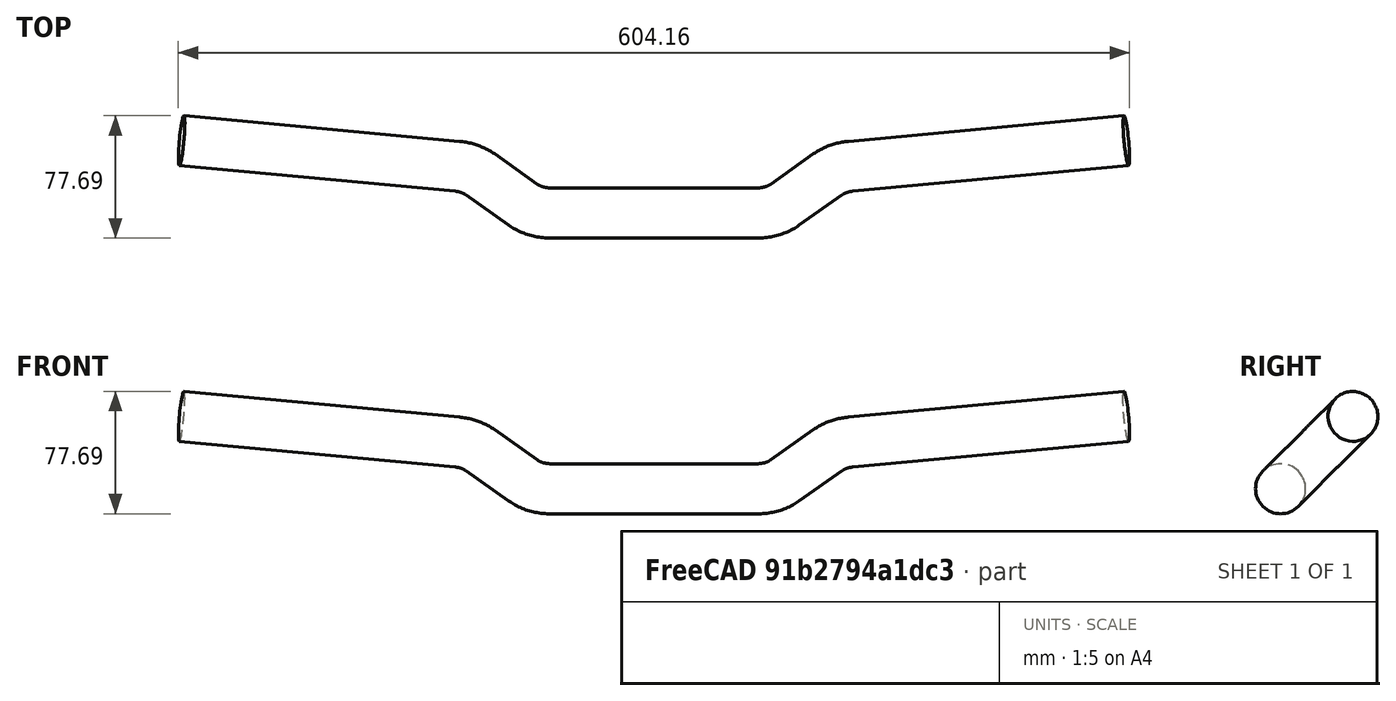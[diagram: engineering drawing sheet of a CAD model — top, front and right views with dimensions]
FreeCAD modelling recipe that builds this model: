
FCSTD DOCUMENT  (FreeCAD 0.20R27319 (Git))
Label: Riserbar_Single
License: All rights reserved
LicenseURL: http://en.wikipedia.org/wiki/All_rights_reserved
objects: Sketcher::SketchObject×2, PartDesign::AdditivePipe×1, PartDesign::Line×1, PartDesign::Plane×1, PartDesign::Body×1
note: 7 computed .brp shape members not serialized (recipe doc carries the construction recipe); baked Part::Feature solids carry a one-line shape summary decoded from their .brp

FEATURE [Sketcher::SketchObject] Sketch001  label="Profil"
  FullyConstrained = true
  MapMode = 5
  Placement = pos=(0,0,0) rot=(0.57735,0.57735,0.57735;2.0944rad)
  Support = -> [YZ_Plane]
  sketch-geometry (1):
    g0: Circle CenterX=0 CenterY=0 CenterZ=0 NormalX=0 NormalY=0 NormalZ=1 AngleXU=0 Radius=15.9
  constraints (2):
    c: Coincident(g0,g-1)
    c: Diameter(g0) = 31.8
FEATURE [Sketcher::SketchObject] Sketch  label="Lenker"
  FullyConstrained = true
  MapMode = 5
  Support = -> [XY_Plane]
  sketch-geometry (11):
    g0: LineSegment StartX=-300 StartY=65 StartZ=0 EndX=-125 EndY=41.9608 EndZ=0
    g1: LineSegment StartX=-110.585 StartY=34.8524 StartZ=0 EndX=-83.0555 EndY=7.32233 EndZ=0
    g2: LineSegment StartX=-65.3778 StartY=0 StartZ=0 EndX=65.3778 EndY=0 EndZ=0
    g3: LineSegment StartX=83.0555 StartY=7.32233 StartZ=0 EndX=110.585 EndY=34.8524 EndZ=0
    g4: LineSegment StartX=125 StartY=41.9608 StartZ=0 EndX=300 EndY=65 EndZ=0
    g5: ArcOfCircle CenterX=-128.263 CenterY=17.1747 CenterZ=0 NormalX=0 NormalY=0 NormalZ=1 AngleXU=0 Radius=25 StartAngle=0.785398 EndAngle=1.4399
    g6: ArcOfCircle CenterX=128.263 CenterY=17.1747 CenterZ=0 NormalX=0 NormalY=0 NormalZ=1 AngleXU=0 Radius=25 StartAngle=1.7017 EndAngle=2.35619
    g7: ArcOfCircle CenterX=-65.3778 CenterY=25 CenterZ=0 NormalX=0 NormalY=0 NormalZ=1 AngleXU=0 Radius=25 StartAngle=3.92699 EndAngle=4.71239
    g8: ArcOfCircle CenterX=65.3778 CenterY=25 CenterZ=0 NormalX=0 NormalY=0 NormalZ=1 AngleXU=0 Radius=25 StartAngle=4.71239 EndAngle=5.49779
    g9: LineSegment StartX=300 StartY=65 StartZ=0 EndX=-300 EndY=65 EndZ=0
    g10: LineSegment StartX=-125 StartY=41.9608 StartZ=0 EndX=125 EndY=41.9608 EndZ=0
  constraints (26):
    c: PointOnObject(g-1,g2)
    c: Symmetric(g0,g4,g-2)
    c: DistanceX(g0,g4) = 600
    c: Tangent(g0,g5) = 1.5708
    c: Tangent(g1,g5) = 1.5708
    c: Tangent(g3,g6) = 1.5708
    c: Tangent(g4,g6) = 1.5708
    c: Symmetric(g6,g5,g-2)
    c: Tangent(g1,g7) = -1.5708
    c: Tangent(g2,g7) = -1.5708
    c: Tangent(g2,g8) = -1.5708
    c: Tangent(g3,g8) = -1.5708
    c: Symmetric(g8,g7,g-2)
    c: Horizontal(g2)
    c: Coincident(g9,g4)
    c: Coincident(g9,g0)
    c: Coincident(g10,g0)
    c: Horizontal(g10)
    c: Coincident(g4,g10)
    c: Distance(g5,g1) = 25
    c: DistanceY(g2,g7) = 25
    c: DistanceX(g10,g10) = 250
    c: Angle(g0,g9) = 0.1309
    c: Angle(g3,g2) = 2.35619
    c: DistanceY(g-1,g4) = 65
    c: DistanceX(g2,g2) = 130.756
FEATURE [PartDesign::AdditivePipe] AdditivePipe
  AuxilleryCurvelinear = true
  AuxillerySpineTangent = false
  Binormal = (0,0,0)
  Mode = 0
  Placement = pos=(0,0,0) rot=(0.57735,0.57735,0.57735;2.0944rad)
  Profile = -> Sketch001
  Spine = -> Sketch
  SpineTangent = false
  Transformation = 0
  Transition = 0
FEATURE [PartDesign::Line] Axis_1  label="Axis_Main"
  AttacherType = Attacher::AttachEngineLine
  Length = 200
  MapMode = 42
  Placement = pos=(0,7.55e-14,4e-16) rot=(0.57735,0.57735,0.57735;2.0944rad)
  ResizeMode = 1
  Support = -> [Sketch001]
FEATURE [PartDesign::Plane] Plane_1  label="Plane_Sym"
  Length = 100
  MapMode = 45
  Placement = pos=(0,7.55e-14,4e-16) rot=(0.57735,0.57735,0.57735;2.0944rad)
  ResizeMode = 1
  Support = -> [Sketch001]
  Width = 100
FEATURE [PartDesign::Body] Body  label="Riserbar"
  Group = -> [Sketch,Sketch001,AdditivePipe,Axis_1,Plane_1]
  Origin = -> Origin
  Placement = pos=(0,0,0) rot=(1,0,0;0.785398rad)
  Tip = -> AdditivePipe
